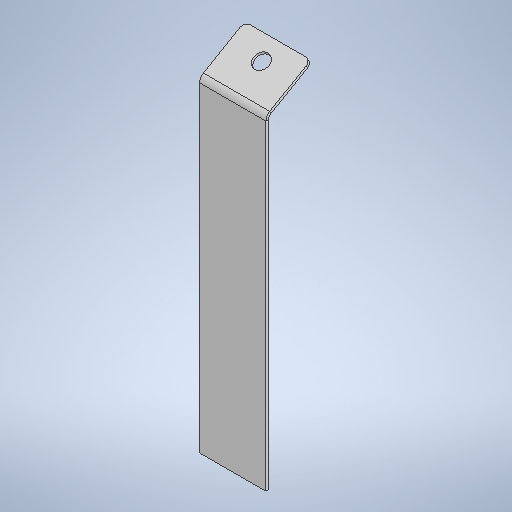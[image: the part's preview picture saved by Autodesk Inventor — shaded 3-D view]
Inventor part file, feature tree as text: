
AUTODESK INVENTOR PART (.ipt)
format: ipt  version: 2025 (Build 290162010, 162A)  size: 304,128 bytes
history: native  units: mm
features: sheet_metal_op x4, other x4, sketch x3, chamfer x1
ambient origin geometry x8: Origin, YZ Plane, XZ Plane, XY Plane, X Axis, Y Axis, Z Axis, Center Point
bodies: Solid1 (feature_tree)
feature tree (12):
  sheet_metal_op  "Face1"
  sheet_metal_op  "Flange1"
  chamfer  "Corner Round1"
  sketch  "Sketch1"  dims[d6=3.0mm]
  other  "Plate1"
  sketch  "Sketch2"  dims[d7=70.0mm]
  other  "Plate2"
  sheet_metal_op  "Bend1"
  sheet_metal_op  "Corner1"
  sketch  "Sketch3"  dims[d8=343.0mm d9=3.0mm d10=1.5mm d11=6.0mm d12=5.0mm d13=55.0mm d14=60.0deg d15=5.0mm d16=12.0mm d17=3.0mm d18=5.0mm d19=20.0mm d20=16.0mm d21=3.0mm d22=0.0mm d23=6.0mm d24=0.872665mm]
  other  "Cut1"
  other  "Definition1"
